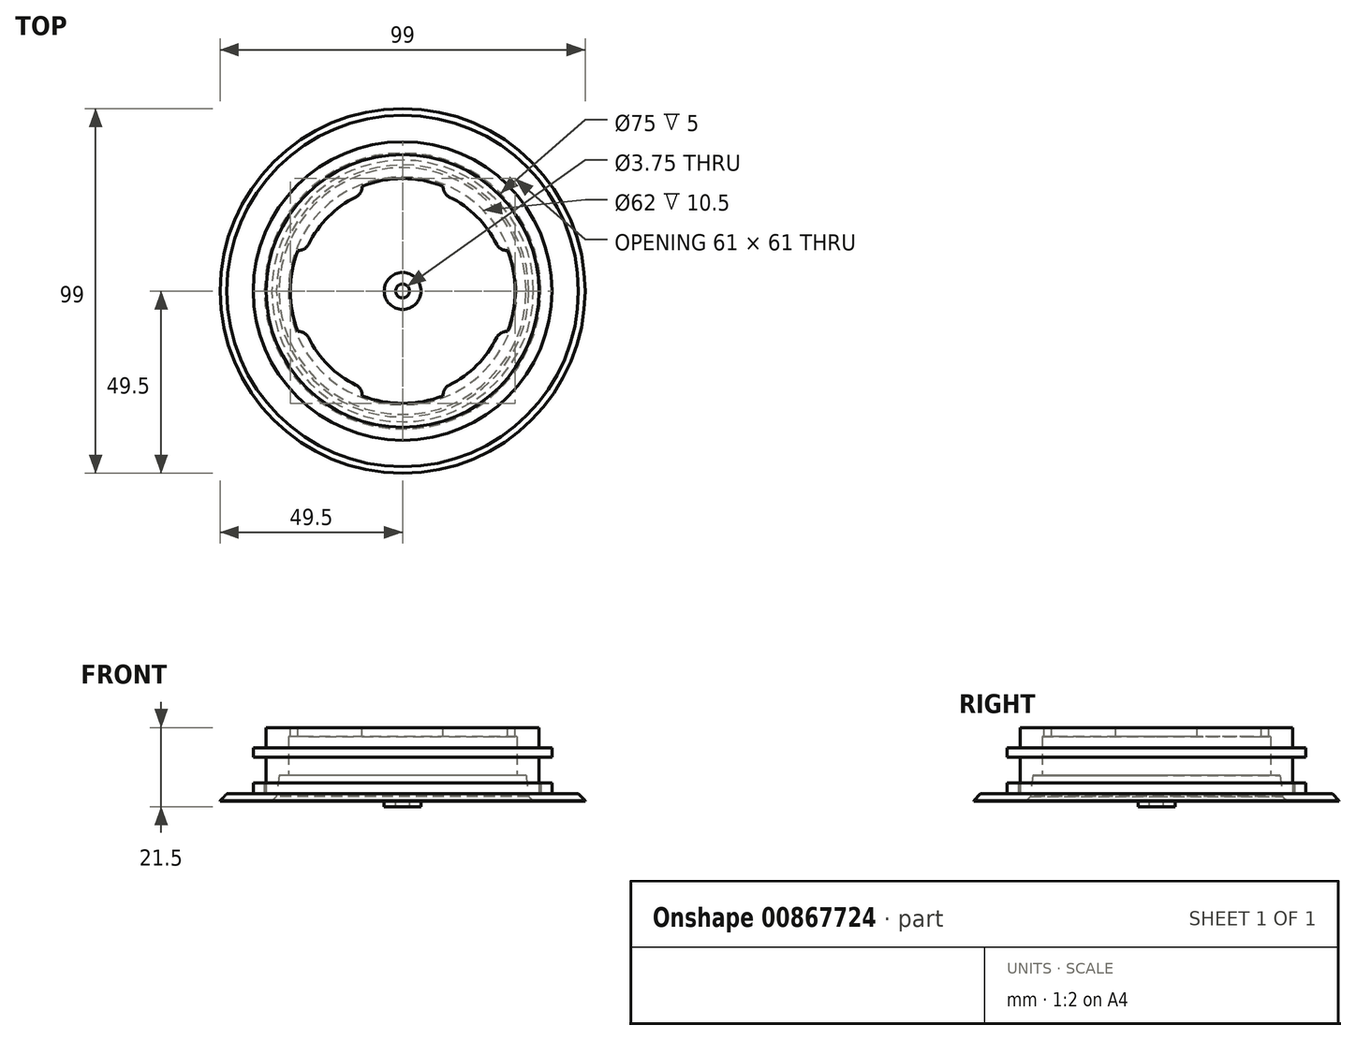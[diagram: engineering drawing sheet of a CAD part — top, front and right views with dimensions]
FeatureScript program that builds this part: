
annotation { "Feature Type Name" : "Feature", "Feature Type Description" : "" }
export const myFeature = defineFeature(function(context is Context, id is Id, definition is map)
    precondition{}
    {
        {
            var Q0;
            Q0=qCreatedBy(makeId("Top.planeOp"),FACE);
            var sketch = newSketch(context, id + "F0", { "sketchPlane" : qUnion([Q0])});
            skCircle(sketch, "E0", {"center": v(0, 0) * mm, "radius": 37 * mm});
            skCircle(sketch, "E1", {"center": v(0, 0) * mm, "radius": 33.5 * mm});
            skSolve(sketch);
        }
        {
            var Q0;
            Q0=makeQuery(id+"F0.imprint","IMPRINT",FACE,{"disambiguationData":[TD([[makeQuery(id+"F0.imprint","IMPRINT",EDGE,{"derivedFrom":sQuery(id+"F0.wireOp",EDGE,"E0")}),1.0]])]});
            extrude(context, id + "F1", {"entities" : qUnion([Q0]), "depth" : 7 * mm, "offsetDistance" : 25 * mm});
        }
        {
            var Q0;
            Q0=makeQuery(id+"F1.opExtrude","CAP_FACE",FACE,{"disambiguationData":[OSD([sQuery(id+"F0.wireOp",EDGE,"E0"),sQuery(id+"F0.wireOp",EDGE,"E1")])],"isStart":false});
            var sketch = newSketch(context, id + "F2", { "sketchPlane" : qUnion([Q0])});
            skCircle(sketch, "E2.0", {"center": v(0, 0) * mm, "radius": 37 * mm});
            skCircle(sketch, "E3.0", {"center": v(0, 0) * mm, "radius": 31 * mm});
            skSolve(sketch);
        }
        {
            var Q0;
            Q0=makeQuery(id+"F2.imprint","IMPRINT",FACE,{"disambiguationData":[TD([[makeQuery(id+"F2.imprint","IMPRINT",EDGE,{"derivedFrom":sQuery(id+"F2.wireOp",EDGE,"E3.0")}),-1.0]])]});
            var Q1;
            Q1=makeQuery(id+"F2.imprint","IMPRINT",FACE,{"disambiguationData":[TD([[makeQuery(id+"F2.imprint","IMPRINT",EDGE,{"derivedFrom":sQuery(id+"F2.wireOp",EDGE,"E2.0")}),1.0]])]});
            extrude(context, id + "F3", {"entities" : qUnion([Q0, Q1]), "operationType" : NewBodyOperationType.ADD, "depth" : 5 * mm, "offsetDistance" : 25 * mm});
        }
        {
            var Q0;
            Q0=makeQuery(id+"F3.opExtrude","CAP_FACE",FACE,{"disambiguationData":[OSD([sQuery(id+"F2.wireOp",EDGE,"E2.0"),sQuery(id+"F2.wireOp",EDGE,"E3.0")])],"isStart":false});
            var sketch = newSketch(context, id + "F4", { "sketchPlane" : qUnion([Q0])});
            skCircle(sketch, "E4.0", {"center": v(0, 0) * mm, "radius": 31 * mm});
            skCircle(sketch, "E5.0", {"center": v(0, 0) * mm, "radius": 37 * mm, "construction": true});
            skCircle(sketch, "E6.0", {"center": v(0, 0) * mm, "radius": 40.5 * mm});
            skSolve(sketch);
        }
        {
            var Q0;
            Q0=makeQuery(id+"F4.imprint","IMPRINT",FACE,{"disambiguationData":[TD([[makeQuery(id+"F4.imprint","IMPRINT",EDGE,{"derivedFrom":sQuery(id+"F4.wireOp",EDGE,"E6.0")}),1.0]])]});
            var Q1;
            Q1=makeQuery(id+"F4.imprint","IMPRINT",FACE,{"disambiguationData":[TD([[makeQuery(id+"F4.imprint","IMPRINT",EDGE,{"derivedFrom":sQuery(id+"F4.wireOp",EDGE,"E4.0")}),-1.0]])]});
            extrude(context, id + "F5", {"entities" : qUnion([Q0, Q1]), "operationType" : NewBodyOperationType.ADD, "depth" : 2.5 * mm, "offsetDistance" : 25 * mm});
        }
        {
            var Q0;
            Q0=makeQuery(id+"F5.opExtrude","CAP_FACE",FACE,{"disambiguationData":[OSD([sQuery(id+"F4.wireOp",EDGE,"E4.0"),sQuery(id+"F4.wireOp",EDGE,"E6.0")])],"isStart":false});
            var sketch = newSketch(context, id + "F6", { "sketchPlane" : qUnion([Q0])});
            skCircle(sketch, "E7.0", {"center": v(0, 0) * mm, "radius": 31 * mm});
            skCircle(sketch, "E8.0", {"center": v(0, 0) * mm, "radius": 37 * mm});
            skSolve(sketch);
        }
        {
            var Q0;
            Q0=makeQuery(id+"F6.imprint","IMPRINT",FACE,{"disambiguationData":[TD([[makeQuery(id+"F6.imprint","IMPRINT",EDGE,{"derivedFrom":sQuery(id+"F6.wireOp",EDGE,"E7.0")}),-1.0]])]});
            extrude(context, id + "F7", {"entities" : qUnion([Q0]), "operationType" : NewBodyOperationType.ADD, "depth" : 5.5 * mm, "offsetDistance" : 25 * mm});
        }
        {
            var Q0;
            Q0=makeQuery(id+"F7.opExtrude","CAP_FACE",FACE,{"disambiguationData":[OSD([sQuery(id+"F6.wireOp",EDGE,"E7.0"),sQuery(id+"F6.wireOp",EDGE,"E8.0")])],"isStart":false});
            var sketch = newSketch(context, id + "F8", { "sketchPlane" : qUnion([Q0])});
            skCircle(sketch, "E9.0", {"center": v(0, 0) * mm, "radius": 37 * mm});
            skArc(sketch, "E10.0", {"start": v(-12.67, 25.53) * mm, "mid": v(-20.15, 20.15) * mm, "end": v(-25.53, 12.67) * mm});
            skArc(sketch, "E11.0", {"start": v(-28.45, 11) * mm, "mid": v(-30.5, 0) * mm, "end": v(-28.45, -11) * mm});
            skLineSegment(sketch, "E12", {"start": v(0, 0) * mm, "end": v(0, 37) * mm, "construction": true});
            skLineSegment(sketch, "E13.0", {"start": v(11, 28.22) * mm, "end": v(11, 28.45) * mm});
            skLineSegment(sketch, "E14.0", {"start": v(-11, 28.22) * mm, "end": v(-11, 28.45) * mm});
            skLineSegment(sketch, "E15.1.0", {"start": v(-28.22, -11) * mm, "end": v(-28.45, -11) * mm});
            skLineSegment(sketch, "E15.1.1", {"start": v(-28.22, 11) * mm, "end": v(-28.45, 11) * mm});
            skLineSegment(sketch, "E15.2.0", {"start": v(11, -28.22) * mm, "end": v(11, -28.45) * mm});
            skLineSegment(sketch, "E15.2.1", {"start": v(-11, -28.22) * mm, "end": v(-11, -28.45) * mm});
            skLineSegment(sketch, "E16.1.3.0", {"start": v(28.22, 11) * mm, "end": v(28.45, 11) * mm});
            skLineSegment(sketch, "E16.3.3.0", {"start": v(28.22, -11) * mm, "end": v(28.45, -11) * mm});
            skArc(sketch, "E17.trimOffspring", {"start": v(25.53, 12.67) * mm, "mid": v(20.15, 20.15) * mm, "end": v(12.67, 25.53) * mm});
            skArc(sketch, "E18.trimOffspring", {"start": v(12.67, -25.53) * mm, "mid": v(20.15, -20.15) * mm, "end": v(25.53, -12.67) * mm});
            skArc(sketch, "E19.trimOffspring", {"start": v(-25.53, -12.67) * mm, "mid": v(-20.15, -20.15) * mm, "end": v(-12.67, -25.53) * mm});
            skArc(sketch, "E20.trimOffspring", {"start": v(11, 28.45) * mm, "mid": v(0, 30.5) * mm, "end": v(-11, 28.45) * mm});
            skArc(sketch, "E21.trimOffspring", {"start": v(28.45, -11) * mm, "mid": v(30.5, 0) * mm, "end": v(28.45, 11) * mm});
            skArc(sketch, "E22.trimOffspring", {"start": v(-11, -28.45) * mm, "mid": v(0, -30.5) * mm, "end": v(11, -28.45) * mm});
            skPoint(sketch, "E23.visualSharp", {"position": v(-26.3, 11) * mm});
            skArc(sketch, "E23.filletArc", {"start": v(-28.22, 11) * mm, "mid": v(-26.64, 11.45) * mm, "end": v(-25.53, 12.67) * mm});
            skPoint(sketch, "E24.visualSharp", {"position": v(-26.3, -11) * mm});
            skArc(sketch, "E24.filletArc", {"start": v(-25.53, -12.67) * mm, "mid": v(-26.64, -11.45) * mm, "end": v(-28.22, -11) * mm});
            skPoint(sketch, "E25.visualSharp", {"position": v(-11, -26.3) * mm});
            skArc(sketch, "E25.filletArc", {"start": v(-11, -28.22) * mm, "mid": v(-11.45, -26.64) * mm, "end": v(-12.67, -25.53) * mm});
            skPoint(sketch, "E26.visualSharp", {"position": v(11, -26.3) * mm});
            skArc(sketch, "E26.filletArc", {"start": v(12.67, -25.53) * mm, "mid": v(11.45, -26.64) * mm, "end": v(11, -28.22) * mm});
            skPoint(sketch, "E27.visualSharp", {"position": v(26.3, -11) * mm});
            skArc(sketch, "E27.filletArc", {"start": v(28.22, -11) * mm, "mid": v(26.64, -11.45) * mm, "end": v(25.53, -12.67) * mm});
            skPoint(sketch, "E28.visualSharp", {"position": v(26.3, 11) * mm});
            skArc(sketch, "E28.filletArc", {"start": v(25.53, 12.67) * mm, "mid": v(26.64, 11.45) * mm, "end": v(28.22, 11) * mm});
            skPoint(sketch, "E29.visualSharp", {"position": v(11, 26.3) * mm});
            skArc(sketch, "E29.filletArc", {"start": v(11, 28.22) * mm, "mid": v(11.45, 26.64) * mm, "end": v(12.67, 25.53) * mm});
            skPoint(sketch, "E30.visualSharp", {"position": v(-11, 26.3) * mm});
            skArc(sketch, "E30.filletArc", {"start": v(-12.67, 25.53) * mm, "mid": v(-11.45, 26.64) * mm, "end": v(-11, 28.22) * mm});
            skSolve(sketch);
        }
        {
            var Q0;
            Q0=makeQuery(id+"F8.imprint","IMPRINT",FACE,{"disambiguationData":[TD([[makeQuery(id+"F8.imprint","IMPRINT",EDGE,{"derivedFrom":sQuery(id+"F8.wireOp",EDGE,"E10.0")}),-1.0]])]});
            extrude(context, id + "F9", {"entities" : qUnion([Q0]), "operationType" : NewBodyOperationType.ADD, "oppositeDirection" : true, "depth" : 2.5 * mm, "offsetDistance" : 25 * mm});
        }
        {
            var Q0;
            Q0=makeQuery(id+"F1.opExtrude","CAP_EDGE",EDGE,{"disambiguationData":[OSD([sQuery(id+"F0.wireOp",EDGE,"E1")])],"isStart":true});
            chamfer(context, id + "F10", {"entities" : qUnion([Q0]), "width" : 2 * mm, "tangentPropagation" : true});
        }
        {
            var Q0;
            Q0=qCreatedBy(makeId("Top.planeOp"),FACE);
            var sketch = newSketch(context, id + "F11", { "sketchPlane" : qUnion([Q0])});
            skCircle(sketch, "E31", {"center": v(0, 0) * mm, "radius": 1.88 * mm});
            skCircle(sketch, "E32", {"center": v(0, 0) * mm, "radius": 5 * mm});
            skSolve(sketch);
        }
        {
            var Q0;
            Q0 = qSketchRegion(id + "F11", true);
            extrude(context, id + "F12", {"entities" : qUnion([Q0]), "oppositeDirection" : true, "depth" : 1.5 * mm, "offsetDistance" : 25 * mm});
        }
        {
            var Q0;
            Q0=makeQuery(id+"F1.opExtrude","CAP_FACE",FACE,{"disambiguationData":[OSD([sQuery(id+"F0.wireOp",EDGE,"E0"),sQuery(id+"F0.wireOp",EDGE,"E1")])],"isStart":true});
            var sketch = newSketch(context, id + "F13", { "sketchPlane" : qUnion([Q0])});
            skCircle(sketch, "E33.0", {"center": v(0, 0) * mm, "radius": 37 * mm, "construction": true});
            skCircle(sketch, "E34.0", {"center": v(0, 0) * mm, "radius": 37.5 * mm});
            skCircle(sketch, "E35.0", {"center": v(0, 0) * mm, "radius": 49.5 * mm});
            skSolve(sketch);
        }
        {
            var Q0;
            Q0=makeQuery(id+"F13.imprint","IMPRINT",FACE,{"disambiguationData":[TD([[makeQuery(id+"F13.imprint","IMPRINT",EDGE,{"derivedFrom":sQuery(id+"F13.wireOp",EDGE,"E34.0")}),-1.0]])]});
            extrude(context, id + "F14", {"entities" : qUnion([Q0]), "oppositeDirection" : true, "depth" : 2 * mm, "offsetDistance" : 25 * mm});
        }
        {
            var Q0;
            Q0=makeQuery(id+"F14.opExtrude","CAP_FACE",FACE,{"disambiguationData":[OSD([sQuery(id+"F13.wireOp",EDGE,"E34.0"),sQuery(id+"F13.wireOp",EDGE,"E35.0")])],"isStart":false});
            var sketch = newSketch(context, id + "F15", { "sketchPlane" : qUnion([Q0])});
            skCircle(sketch, "E36.0", {"center": v(0, 0) * mm, "radius": 37.5 * mm});
            skCircle(sketch, "E37.0", {"center": v(0, 0) * mm, "radius": 40.5 * mm});
            skSolve(sketch);
        }
        {
            var Q0;
            Q0=makeQuery(id+"F15.imprint","IMPRINT",FACE,{"disambiguationData":[TD([[makeQuery(id+"F15.imprint","IMPRINT",EDGE,{"derivedFrom":sQuery(id+"F15.wireOp",EDGE,"E36.0")}),1.0]])]});
            extrude(context, id + "F16", {"entities" : qUnion([Q0]), "operationType" : NewBodyOperationType.ADD, "depth" : 3 * mm, "offsetDistance" : 25 * mm});
        }
        {
            var Q0;
            Q0=makeQuery(id+"F14.opExtrude","CAP_EDGE",EDGE,{"disambiguationData":[OSD([sQuery(id+"F13.wireOp",EDGE,"E35.0")])],"isStart":false});
            chamfer(context, id + "F17", {"entities" : qUnion([Q0]), "width" : 1.8 * mm, "tangentPropagation" : true});
        }
        {
            var Q0;
            {var subQ0=sQuery(id+"F0.wireOp",EDGE,"E1");Q0=makeQuery(id+"F10.opChamfer","BLEND_EDGE",EDGE,{"blendedFrom":[makeQuery(id+"F1.opExtrude","CAP_EDGE",EDGE,{"disambiguationData":[OSD([subQ0])],"isStart":true}),makeQuery(id+"F1.opExtrude","SWEPT_FACE",FACE,{"disambiguationData":[OSD([subQ0])]})],"blendedInto":[makeQuery(id+"F1.opExtrude","SWEPT_FACE",FACE,{"disambiguationData":[OSD([subQ0])]})]});}
            chamfer(context, id + "F18", {"entities" : qUnion([Q0]), "chamferType" : ChamferType.TWO_OFFSETS, "width1" : 5 * mm, "oppositeDirection" : false, "width2" : 1 * mm, "tangentPropagation" : true});
        }
    });
